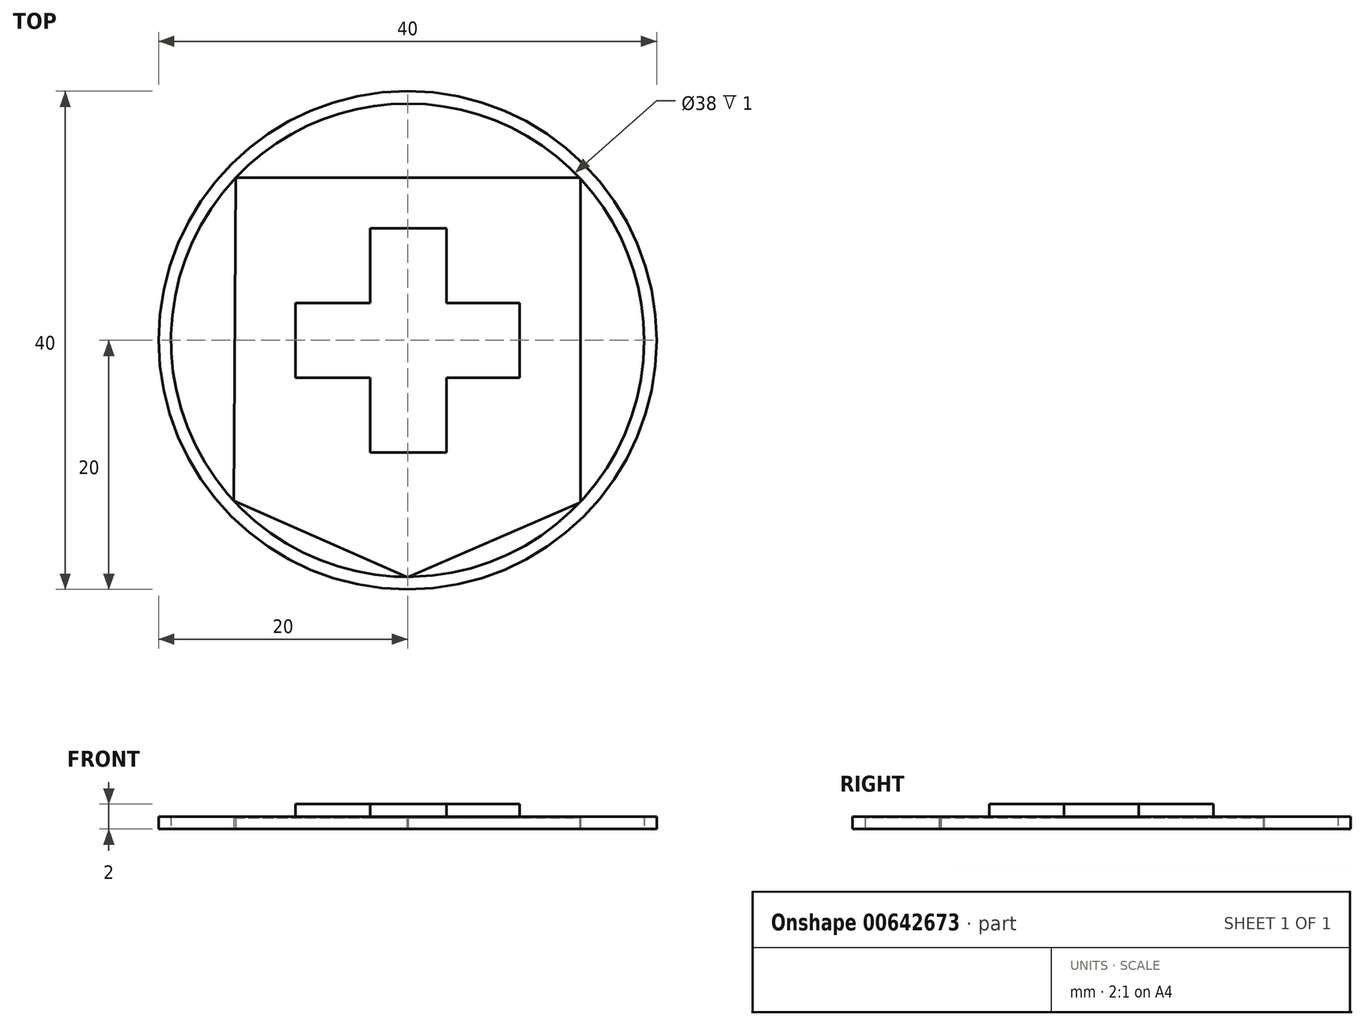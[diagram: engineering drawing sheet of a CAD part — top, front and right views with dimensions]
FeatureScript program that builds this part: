
annotation { "Feature Type Name" : "Feature", "Feature Type Description" : "" }
export const myFeature = defineFeature(function(context is Context, id is Id, definition is map)
    precondition{}
    {
        {
            var Q0;
            Q0=qCreatedBy(makeId("Top.planeOp"),FACE);
            var sketch = newSketch(context, id + "F0", { "sketchPlane" : qUnion([Q0])});
            skCircle(sketch, "E0", {"center": v(0, 0) * mm, "radius": 20 * mm});
            skCircle(sketch, "E1", {"center": v(0, 0) * mm, "radius": 19 * mm});
            skSolve(sketch);
        }
        {
            var Q0;
            Q0=makeQuery(id+"F0.imprint","IMPRINT",FACE,{"disambiguationData":[TD([[makeQuery(id+"F0.imprint","IMPRINT",EDGE,{"derivedFrom":sQuery(id+"F0.wireOp",EDGE,"E0")}),1.0]])]});
            extrude(context, id + "F1", {"entities" : qUnion([Q0]), "depth" : 1 * mm, "offsetDistance" : 25 * mm});
        }
        {
            var Q0;
            Q0=qCreatedBy(makeId("Top.planeOp"),FACE);
            var sketch = newSketch(context, id + "F2", { "sketchPlane" : qUnion([Q0])});
            skLineSegment(sketch, "E2", {"start": v(-13.82, 13.05) * mm, "end": v(13.87, 13.05) * mm});
            skLineSegment(sketch, "E3", {"start": v(13.87, 13.05) * mm, "end": v(13.87, -13.01) * mm});
            skLineSegment(sketch, "E4", {"start": v(13.87, -13.01) * mm, "end": v(0, -19.02) * mm});
            skLineSegment(sketch, "E5", {"start": v(-13.95, -12.88) * mm, "end": v(-13.82, 13.05) * mm});
            skLineSegment(sketch, "E6", {"start": v(-13.95, -12.88) * mm, "end": v(0, -19.02) * mm});
            skSolve(sketch);
        }
        {
            var Q0;
            Q0=qCreatedBy(makeId("Top.planeOp"),FACE);
            var sketch = newSketch(context, id + "F3", { "sketchPlane" : qUnion([Q0])});
            skLineSegment(sketch, "E7", {"start": v(0, 0) * mm, "end": v(3, 0) * mm});
            skLineSegment(sketch, "E8", {"start": v(3, 0) * mm, "end": v(0, 0) * mm});
            skLineSegment(sketch, "E9", {"start": v(0, 0) * mm, "end": v(-3, 0) * mm});
            skLineSegment(sketch, "E10.bottom", {"start": v(-3, 0) * mm, "end": v(3.1, 0) * mm});
            skLineSegment(sketch, "E10.top", {"start": v(-3, 9) * mm, "end": v(3.1, 9) * mm});
            skLineSegment(sketch, "E10.left", {"start": v(-3, 0) * mm, "end": v(-3, 9) * mm});
            skLineSegment(sketch, "E10.right", {"start": v(3.1, 0) * mm, "end": v(3.1, 9) * mm});
            skLineSegment(sketch, "E11", {"start": v(0, 0) * mm, "end": v(0, 3) * mm});
            skLineSegment(sketch, "E12", {"start": v(0, 3) * mm, "end": v(0, 0) * mm});
            skLineSegment(sketch, "E13", {"start": v(0, 0) * mm, "end": v(0, -3) * mm});
            skLineSegment(sketch, "E14.bottom", {"start": v(0, 3) * mm, "end": v(9, 3) * mm});
            skLineSegment(sketch, "E14.top", {"start": v(0, -3) * mm, "end": v(9, -3) * mm});
            skLineSegment(sketch, "E14.left", {"start": v(0, 3) * mm, "end": v(0, -3) * mm});
            skLineSegment(sketch, "E14.right", {"start": v(9, 3) * mm, "end": v(9, -3) * mm});
            skLineSegment(sketch, "E15.bottom", {"start": v(0, -3) * mm, "end": v(-9, -3) * mm});
            skLineSegment(sketch, "E15.top", {"start": v(0, 3) * mm, "end": v(-9, 3) * mm});
            skLineSegment(sketch, "E15.left", {"start": v(0, -3) * mm, "end": v(0, 3) * mm});
            skLineSegment(sketch, "E15.right", {"start": v(-9, -3) * mm, "end": v(-9, 3) * mm});
            skLineSegment(sketch, "E16.top", {"start": v(-3, -9) * mm, "end": v(3.1, -9) * mm});
            skLineSegment(sketch, "E16.left", {"start": v(-3, 0) * mm, "end": v(-3, -9) * mm});
            skLineSegment(sketch, "E16.right", {"start": v(3.1, 0) * mm, "end": v(3.1, -9) * mm});
            skLineSegment(sketch, "E17", {"start": v(0, -3) * mm, "end": v(0, -3) * mm});
            skLineSegment(sketch, "E18", {"start": v(0, -3) * mm, "end": v(0.02, -3.14) * mm});
            skSolve(sketch);
        }
        {
            var Q0;
            Q0 = qSketchRegion(id + "F3", true);
            extrude(context, id + "F4", {"entities" : qUnion([Q0]), "depth" : 2 * mm, "offsetDistance" : 25 * mm});
        }
        {
            var Q0;
            Q0=makeQuery(id+"F2.imprint","IMPRINT",FACE,{"disambiguationData":[TD([[makeQuery(id+"F2.imprint","IMPRINT",EDGE,{"derivedFrom":sQuery(id+"F2.wireOp",EDGE,"E2")}),-1.0]])]});
            extrude(context, id + "F5", {"entities" : qUnion([Q0]), "operationType" : NewBodyOperationType.ADD, "depth" : 0.9 * mm, "offsetDistance" : 25 * mm});
        }
    });
